# Revit family: H_ww_BIM_FP-10B_de_DE_0718
name_source: partatom
category: Sonderausstattung
revit_build: Autodesk Revit 2016 (Build: 20161004_0715(x64)
units: mm (PartAtom-declared; Revit-internal decimal feet)

## family parameters
Arbeitsebenenbasiert = Nein
Beim Laden mit Abzugskörper schneiden = Nein
Bemaßung runder Anschluss = Durchmesser verwenden
Gemeinsam genutzt = Nein
Immer vertikal = Ja
Raumberechnungspunkt = Nein
Teiletyp = Normal

## types (1)
- H_ww_BIM_FP-10B_de_DE_0718
    Beschreibung = Undercounter dishwasher
    CE Approved = Ja
    Cold Water Flow = 5 l/min
    Cold Water Maximum Pressure = 10 bar
    Cold Water Minimum Pressure = 0.5 bar
    Cold Water Quality = 0-1.25 clark (0.2 mmol/l)  /  80 µs/cm
    Cold Water Size = 3/4"
    Cold water consumption / rack = 1.00 l
    Cycle = 50 Hz
    Depth Actual = 603 mm
    Depth with open doors = 1048 mm
    Direct Waste Size = 1"
    Electric power = 6800 W
    FL Amps = 14 A
    Height Actual = 825 mm
    Hersteller = HOBART GmbH
    Latent Heat Output = 0.2 kW
    Length Actual = 600 mm
    Max Overcurrent Protection = 16 A
    Modell = FP-10B
    Phase = 3
    Potential Equalisation = Ja
    Sensitive Heat Output = 0.7 kW
    URL = www.hobart.de
    Volts = 400 V
    Weight = 60 kg
